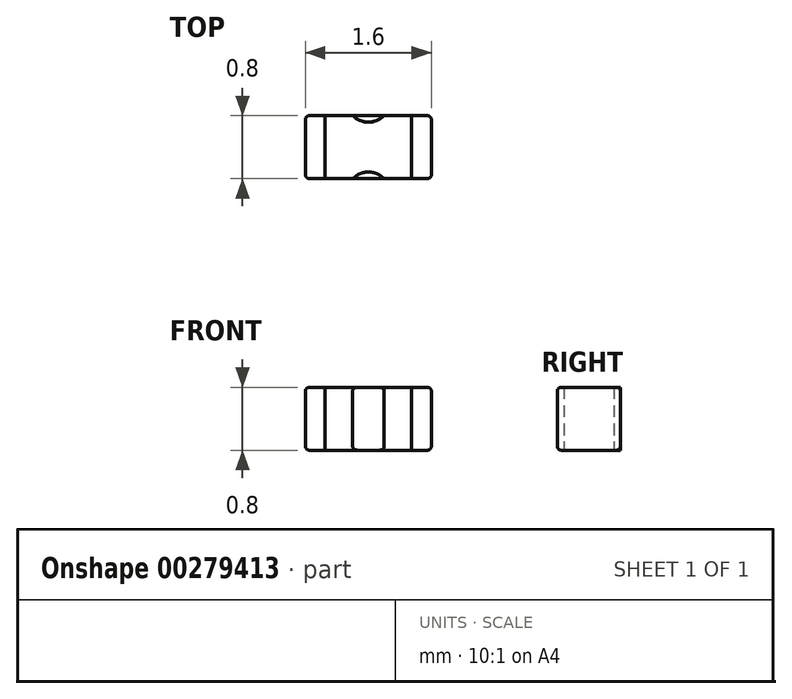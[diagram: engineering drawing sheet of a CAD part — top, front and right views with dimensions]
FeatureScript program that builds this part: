
annotation { "Feature Type Name" : "Feature", "Feature Type Description" : "" }
export const myFeature = defineFeature(function(context is Context, id is Id, definition is map)
    precondition{}
    {
        {
            assignVariable(context, id + "F0", {"name" : "H", "anyValue" : 0.8});
        }
        {
            var Q0;
            Q0=qCreatedBy(makeId("Top.planeOp"),FACE);
            var sketch = newSketch(context, id + "F1", { "sketchPlane" : qUnion([Q0])});
            skLineSegment(sketch, "E0.bottom", {"start": v(0.55, 0.4) * mm, "end": v(-0.55, 0.4) * mm});
            skLineSegment(sketch, "E0.top", {"start": v(0.55, -0.4) * mm, "end": v(-0.55, -0.4) * mm});
            skLineSegment(sketch, "E0.left", {"start": v(0.55, 0.4) * mm, "end": v(0.55, -0.4) * mm});
            skLineSegment(sketch, "E0.right", {"start": v(-0.55, 0.4) * mm, "end": v(-0.55, -0.4) * mm});
            skPoint(sketch, "E0.middle", {"position": v(0, 0) * mm});
            skLineSegment(sketch, "E1", {"start": v(-0.55, 0.4) * mm, "end": v(-0.8, 0.4) * mm});
            skLineSegment(sketch, "E2", {"start": v(-0.8, 0.4) * mm, "end": v(-0.8, -0.4) * mm});
            skLineSegment(sketch, "E3", {"start": v(-0.8, -0.4) * mm, "end": v(-0.55, -0.4) * mm});
            skLineSegment(sketch, "E4", {"start": v(0.55, -0.4) * mm, "end": v(0.8, -0.4) * mm});
            skLineSegment(sketch, "E5", {"start": v(0.8, -0.4) * mm, "end": v(0.8, 0.4) * mm});
            skLineSegment(sketch, "E6", {"start": v(0.8, 0.4) * mm, "end": v(0.55, 0.4) * mm});
            skArc(sketch, "E7", {"start": v(-0.2, 0.4) * mm, "mid": v(0, 0.32) * mm, "end": v(0.2, 0.4) * mm});
            skArc(sketch, "E8", {"start": v(0.2, -0.4) * mm, "mid": v(0, -0.32) * mm, "end": v(-0.2, -0.4) * mm});
            skPoint(sketch, "E9", {"position": v(0, -0.4) * mm});
            skSolve(sketch);
        }
        {
            var Q0;
            {var subQ3=sQuery(id+"F1.wireOp",EDGE,"E0.left");Q0=makeQuery(id+"F1.imprint","IMPRINT",FACE,{"disambiguationData":[TD([[makeQuery(id+"F1.imprint","IMPRINT",EDGE,{"derivedFrom":subQ3}),-1.0]])]});}
            extrude(context, id + "F2", {"entities" : qUnion([Q0]), "depth" : (getVariable(context, 'H')) * mm});
        }
        {
            var Q0;
            Q0=makeQuery(id+"F1.imprint","IMPRINT",FACE,{"disambiguationData":[TD([[makeQuery(id+"F1.imprint","IMPRINT",EDGE,{"derivedFrom":sQuery(id+"F1.wireOp",EDGE,"E0.right")}),-1.0]])]});
            var Q1;
            Q1=makeQuery(id+"F1.imprint","IMPRINT",FACE,{"disambiguationData":[TD([[makeQuery(id+"F1.imprint","IMPRINT",EDGE,{"derivedFrom":sQuery(id+"F1.wireOp",EDGE,"E0.left")}),1.0]])]});
            extrude(context, id + "F3", {"entities" : qUnion([Q0, Q1]), "depth" : (getVariable(context, 'H')) * mm});
        }
        {
            var Q0;
            {var subQ0=sQuery(id+"F1.wireOp",EDGE,"E8");Q0=makeQuery(id+"F1.imprint","IMPRINT",FACE,{"disambiguationData":[TD([[makeQuery(id+"F1.imprint","IMPRINT",EDGE,{"derivedFrom":subQ0}),1.0]])]});}
            var Q1;
            {var subQ0=sQuery(id+"F1.wireOp",EDGE,"E7");Q1=makeQuery(id+"F1.imprint","IMPRINT",FACE,{"disambiguationData":[TD([[makeQuery(id+"F1.imprint","IMPRINT",EDGE,{"derivedFrom":subQ0}),1.0]])]});}
            extrude(context, id + "F4", {"entities" : qUnion([Q0, Q1]), "depth" : (getVariable(context, 'H')) * mm});
        }
        {
            var Q0;
            Q0=makeQuery(id+"F3.opExtrude","SWEPT_FACE",FACE,{"disambiguationData":[OSD([sQuery(id+"F1.wireOp",EDGE,"E2")])]});
            var Q1;
            Q1=makeQuery(id+"F3.opExtrude","SWEPT_FACE",FACE,{"disambiguationData":[OSD([sQuery(id+"F1.wireOp",EDGE,"E5")])]});
            var Q2;
            Q2=makeQuery(id+"F3.opExtrude","CAP_EDGE",EDGE,{"disambiguationData":[OSD([sQuery(id+"F1.wireOp",EDGE,"E6")])],"isStart":false});
            var Q3;
            {var subQ0=sQuery(id+"F1.wireOp",EDGE,"E0.bottom");Q3=makeQuery(id+"F2.opExtrude","CAP_EDGE",EDGE,{"disambiguationData":[OSD([subQ0]),TDD([makeQuery(id+"F1.imprint","IMPRINT",EDGE,{"disambiguationData":[TD([[makeQuery(id+"F1.imprint","INTERSECT",VERTEX,{"disambiguationData":[OD(1.0)],"derivedFrom":[subQ0,sQuery(id+"F1.wireOp",EDGE,"E7")]}),1.0]])],"derivedFrom":subQ0})])],"isStart":false});}
            var Q4;
            Q4=makeQuery(id+"F4.opExtrude","CAP_EDGE",EDGE,{"disambiguationData":[OSD([sQuery(id+"F1.wireOp",EDGE,"E0.bottom")])],"isStart":false});
            var Q5;
            {var subQ0=sQuery(id+"F1.wireOp",EDGE,"E0.bottom");Q5=makeQuery(id+"F2.opExtrude","CAP_EDGE",EDGE,{"disambiguationData":[OSD([subQ0]),TDD([makeQuery(id+"F1.imprint","IMPRINT",EDGE,{"disambiguationData":[TD([[makeQuery(id+"F1.imprint","INTERSECT",VERTEX,{"disambiguationData":[OD(0.0)],"derivedFrom":[subQ0,sQuery(id+"F1.wireOp",EDGE,"E7")]}),-1.0]])],"derivedFrom":subQ0})])],"isStart":false});}
            var Q6;
            Q6=makeQuery(id+"F3.opExtrude","CAP_EDGE",EDGE,{"disambiguationData":[OSD([sQuery(id+"F1.wireOp",EDGE,"E1")])],"isStart":false});
            var Q7;
            Q7=makeQuery(id+"F3.opExtrude","CAP_EDGE",EDGE,{"disambiguationData":[OSD([sQuery(id+"F1.wireOp",EDGE,"E4")])],"isStart":false});
            var Q8;
            {var subQ0=sQuery(id+"F1.wireOp",EDGE,"E0.top");Q8=makeQuery(id+"F2.opExtrude","CAP_EDGE",EDGE,{"disambiguationData":[OSD([subQ0]),TDD([makeQuery(id+"F1.imprint","IMPRINT",EDGE,{"disambiguationData":[TD([[makeQuery(id+"F1.imprint","INTERSECT",VERTEX,{"disambiguationData":[OD(0.0)],"derivedFrom":[subQ0,sQuery(id+"F1.wireOp",EDGE,"E8")]}),1.0]])],"derivedFrom":subQ0})])],"isStart":false});}
            var Q9;
            Q9=makeQuery(id+"F4.opExtrude","CAP_EDGE",EDGE,{"disambiguationData":[OSD([sQuery(id+"F1.wireOp",EDGE,"E0.top")])],"isStart":false});
            var Q10;
            {var subQ0=sQuery(id+"F1.wireOp",EDGE,"E0.top");Q10=makeQuery(id+"F2.opExtrude","CAP_EDGE",EDGE,{"disambiguationData":[OSD([subQ0]),TDD([makeQuery(id+"F1.imprint","IMPRINT",EDGE,{"disambiguationData":[TD([[makeQuery(id+"F1.imprint","INTERSECT",VERTEX,{"disambiguationData":[OD(1.0)],"derivedFrom":[subQ0,sQuery(id+"F1.wireOp",EDGE,"E8")]}),-1.0]])],"derivedFrom":subQ0})])],"isStart":false});}
            var Q11;
            Q11=makeQuery(id+"F3.opExtrude","CAP_EDGE",EDGE,{"disambiguationData":[OSD([sQuery(id+"F1.wireOp",EDGE,"E3")])],"isStart":false});
            var Q12;
            Q12=makeQuery(id+"F3.opExtrude","CAP_EDGE",EDGE,{"disambiguationData":[OSD([sQuery(id+"F1.wireOp",EDGE,"E6")])],"isStart":true});
            var Q13;
            {var subQ0=sQuery(id+"F1.wireOp",EDGE,"E0.bottom");Q13=makeQuery(id+"F2.opExtrude","CAP_EDGE",EDGE,{"disambiguationData":[OSD([subQ0]),TDD([makeQuery(id+"F1.imprint","IMPRINT",EDGE,{"disambiguationData":[TD([[makeQuery(id+"F1.imprint","INTERSECT",VERTEX,{"disambiguationData":[OD(1.0)],"derivedFrom":[subQ0,sQuery(id+"F1.wireOp",EDGE,"E7")]}),1.0]])],"derivedFrom":subQ0})])],"isStart":true});}
            var Q14;
            Q14=makeQuery(id+"F4.opExtrude","CAP_EDGE",EDGE,{"disambiguationData":[OSD([sQuery(id+"F1.wireOp",EDGE,"E0.bottom")])],"isStart":true});
            var Q15;
            {var subQ0=sQuery(id+"F1.wireOp",EDGE,"E0.bottom");Q15=makeQuery(id+"F2.opExtrude","CAP_EDGE",EDGE,{"disambiguationData":[OSD([subQ0]),TDD([makeQuery(id+"F1.imprint","IMPRINT",EDGE,{"disambiguationData":[TD([[makeQuery(id+"F1.imprint","INTERSECT",VERTEX,{"disambiguationData":[OD(0.0)],"derivedFrom":[subQ0,sQuery(id+"F1.wireOp",EDGE,"E7")]}),-1.0]])],"derivedFrom":subQ0})])],"isStart":true});}
            var Q16;
            {var subQ0=sQuery(id+"F1.wireOp",EDGE,"E0.top");Q16=makeQuery(id+"F2.opExtrude","CAP_EDGE",EDGE,{"disambiguationData":[OSD([subQ0]),TDD([makeQuery(id+"F1.imprint","IMPRINT",EDGE,{"disambiguationData":[TD([[makeQuery(id+"F1.imprint","INTERSECT",VERTEX,{"disambiguationData":[OD(1.0)],"derivedFrom":[subQ0,sQuery(id+"F1.wireOp",EDGE,"E8")]}),-1.0]])],"derivedFrom":subQ0})])],"isStart":true});}
            var Q17;
            Q17=makeQuery(id+"F4.opExtrude","CAP_EDGE",EDGE,{"disambiguationData":[OSD([sQuery(id+"F1.wireOp",EDGE,"E0.top")])],"isStart":true});
            var Q18;
            {var subQ0=sQuery(id+"F1.wireOp",EDGE,"E0.top");Q18=makeQuery(id+"F2.opExtrude","CAP_EDGE",EDGE,{"disambiguationData":[OSD([subQ0]),TDD([makeQuery(id+"F1.imprint","IMPRINT",EDGE,{"disambiguationData":[TD([[makeQuery(id+"F1.imprint","INTERSECT",VERTEX,{"disambiguationData":[OD(0.0)],"derivedFrom":[subQ0,sQuery(id+"F1.wireOp",EDGE,"E8")]}),1.0]])],"derivedFrom":subQ0})])],"isStart":true});}
            var Q19;
            Q19=makeQuery(id+"F3.opExtrude","CAP_EDGE",EDGE,{"disambiguationData":[OSD([sQuery(id+"F1.wireOp",EDGE,"E4")])],"isStart":true});
            var Q20;
            Q20=makeQuery(id+"F3.opExtrude","CAP_EDGE",EDGE,{"disambiguationData":[OSD([sQuery(id+"F1.wireOp",EDGE,"E3")])],"isStart":true});
            var Q21;
            Q21=makeQuery(id+"F3.opExtrude","CAP_EDGE",EDGE,{"disambiguationData":[OSD([sQuery(id+"F1.wireOp",EDGE,"E1")])],"isStart":true});
            fillet(context, id + "F5", {"entities" : qUnion([Q0, Q1, Q2, Q3, Q4, Q5, Q6, Q7, Q8, Q9, Q10, Q11, Q12, Q13, Q14, Q15, Q16, Q17, Q18, Q19, Q20, Q21]), "radius" : 0.05 * mm, "allowEdgeOverflow" : false});
        }
    });
